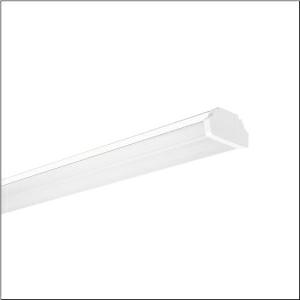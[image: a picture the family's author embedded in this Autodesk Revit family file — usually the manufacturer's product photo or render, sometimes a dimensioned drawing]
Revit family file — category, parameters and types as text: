
# Revit family: dus_r__31_gen_2_53bd8127v485c2_ffde
name_source: partatom
category: Lighting Fixtures
units: mm (PartAtom-declared; Revit-internal decimal feet)

## family parameters
Cut with Voids When Loaded = No
Host = Face
Light Source = No
Part Type = Normal
Room Calculation Point = No
Round Connector Dimension = Use Diameter
Shared = No

## types (1)
- DUS® 31 Gen.2 (1 x LED, 8590 lm, 47.9 W, 4000K)
    Apparent Load = 48 VA
    CIE Flux Codes = 47 80 95 93 100
    Color Rendering = 80
    Color Temperature = 4000K
    Default Elevation = 1800 mm
    Description = DUS® 31 Gen.2, luminaire insert, of sheet steel, coil coated, white, length: 1.535mm, width: 81mm, height: 90mm, 5x system unit, system units: 307mm, LED rated luminous flux: 8.590lm, light colour: 840, control gear: ON/OFF, control gear: ECG, with plug, 3-pole, with phase selection, mains connection: 220..240V, AC, 50/60Hz, rated input power: 48W, through-wiring accessed according to module size, primary optical cover: cover, of PMMA, light emission: direct distribution, primary light characteristic: symmetric, protection rating (complete): IP20, protection rating (LED compartment): IP50, insulation class (complete): insulation class I (protective earthing), certification: CE, ENEC, VDE, UKCA, impact resistance: IK03, permissible ambient temperature for indoor applications: -35..+45°C, corresponds to IFS (International Featured Standards) requirements for safety and quality in the food industry, reducing of maximum allowable ambient temperature of 5°C with ceiling mounting, packaging unit: 1 piece
    Height = 95 mm
    Lamp = 1 x LED
    Lamp Light Flux = 8590 lm
    Lamp Power = 47.9 W
    Lamp count = 1
    Length = 1535 mm
    Luminous efficacy = 179 lm/W
    Manufacturer = Siteco
    ModVariant = No
    Model = 53BD8127V485C2
    Mounting Place = Ceiling
    Mounting Type = Pendant
    Number of Poles = 1
    OnlyDefault = Yes
    Power Factor = 1
    Product Name = DUS® 31 Gen.2
    Product group = luminaire insert
    ProductGroupID = 901
    Protection Class = Protection class I
    Protection Degree = IP 20
    RLX_Detail_Level = 1
    RLX_Emergency_Light_Flux = 0 lm
    RLX_Emergency_Type = 0
    RLX_Emergency_Type_DB = No
    RlxData = <blob elided: 28385 chars, md5=6f720c1c>
    Socket = socket
    Standby Power = 0 W
    System Light Flux = 8590 lm
    System Power = 48 W
    Type Comments = Product without accessories
    Type Image = l_1319596.jpg
    URL = http://relux.com
    VarID = ---
    Voltage = 0 V
    Weight = 0.00 kg
    Width = 81 mm

## geometry (parser evidence)
native form markers: Blend x4, Sweep x12
no freeform markers — native parametric forms only
